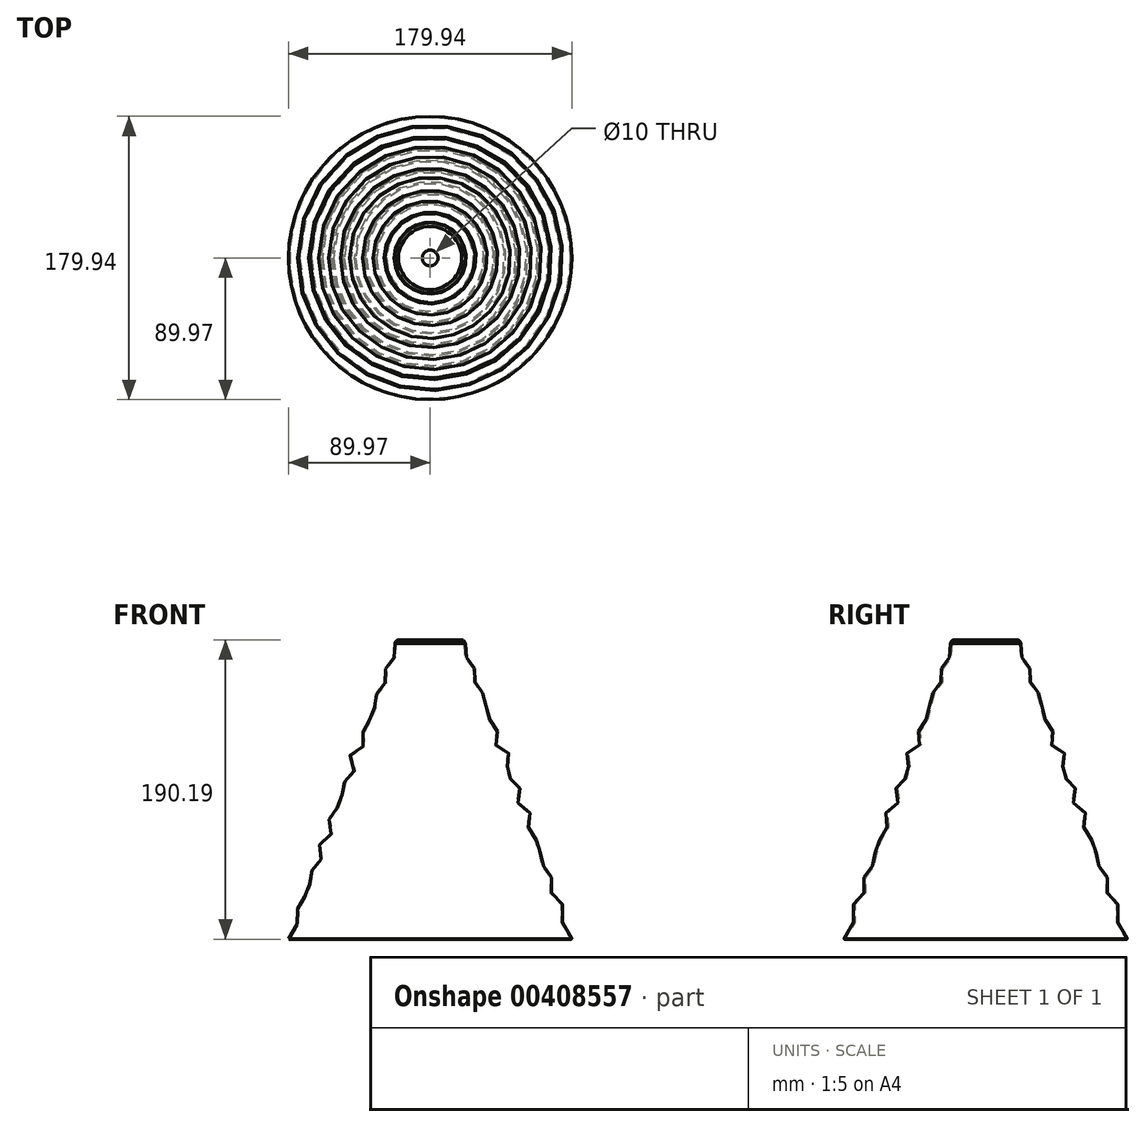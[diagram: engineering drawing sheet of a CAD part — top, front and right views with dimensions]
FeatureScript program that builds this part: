
annotation { "Feature Type Name" : "Feature", "Feature Type Description" : "" }
export const myFeature = defineFeature(function(context is Context, id is Id, definition is map)
    precondition{}
    {
        {
            var Q0;
            Q0=qCreatedBy(makeId("Front.planeOp"),FACE);
            var sketch = newSketch(context, id + "F0", { "sketchPlane" : qUnion([Q0])});
            skLineSegment(sketch, "E0", {"start": v(0, 0) * mm, "end": v(180, 0) * mm, "construction": true});
            skLineSegment(sketch, "E1", {"start": v(180, 0) * mm, "end": v(90, 0) * mm, "construction": true});
            skLineSegment(sketch, "E2", {"start": v(90, 0) * mm, "end": v(90, 190) * mm, "construction": true});
            skLineSegment(sketch, "E3", {"start": v(90, 190) * mm, "end": v(110, 190) * mm, "construction": true});
            skLineSegment(sketch, "E4", {"start": v(90, 190) * mm, "end": v(70, 190) * mm, "construction": true});
            skLineSegment(sketch, "E5", {"start": v(70, 190) * mm, "end": v(85, 190) * mm, "construction": true});
            skLineSegment(sketch, "E6", {"start": v(85, 190) * mm, "end": v(95, 190) * mm, "construction": true});
            skLineSegment(sketch, "E7", {"start": v(70, 190) * mm, "end": v(0, 0) * mm, "construction": true});
            skLineSegment(sketch, "E8", {"start": v(70, 190) * mm, "end": v(90, 244.29) * mm, "construction": true});
            skLineSegment(sketch, "E9", {"start": v(90, 244.29) * mm, "end": v(90, 190) * mm, "construction": true});
            skLineSegment(sketch, "E10", {"start": v(0, 0) * mm, "end": v(0, 244.29) * mm, "construction": true});
            skPoint(sketch, "E11.23.internal.snap0", {"position": v(90, 217.14) * mm});
            skFitSpline(sketch, "E11", {"points": [v(0, 0) * mm, v(6.23, 12.04) * mm, v(6.44, 22.84) * mm, v(13.36, 30.4) * mm, v(13.14, 41.2) * mm, v(20.48, 49.2) * mm, v(19.4, 59.13) * mm, v(27.61, 67.77) * mm, v(25.67, 78.36) * mm, v(34.3, 86.78) * mm, v(33.23, 97.15) * mm, v(41.65, 104.71) * mm, v(39.06, 116.38) * mm, v(48.35, 123.72) * mm, v(47.27, 134.52) * mm, v(54.83, 142.3) * mm, v(53.97, 152.88) * mm, v(61.1, 160.44) * mm, v(61.07, 170.16) * mm, v(66.82, 178.07) * mm, v(67.56, 187.44) * mm, v(73.32, 195.75) * mm, v(73.6, 204.48) * mm, v(82.35, 217.14) * mm, v(81.92, 228.43) * mm, v(87, 236.15) * mm], "startDerivative": vector(195.65, 261.42) * mm, "endDerivative": vector(192.2, 191.7) * mm});
            skLineSegment(sketch, "E12", {"start": v(85, 190) * mm, "end": v(85, 242.54) * mm, "construction": true});
            skFitSpline(sketch, "E13", {"points": [v(67.56, 187.44) * mm, v(68.56, 189.3) * mm, v(70, 190) * mm], "startDerivative": vector(1.51, 4.04) * mm, "endDerivative": vector(3.4, 1) * mm});
            skLineSegment(sketch, "E14", {"start": v(90, 190) * mm, "end": v(90, 170) * mm, "construction": true});
            skLineSegment(sketch, "E15", {"start": v(90, 170) * mm, "end": v(70, 170) * mm, "construction": true});
            skLineSegment(sketch, "E16", {"start": v(70, 170) * mm, "end": v(90, 190) * mm, "construction": true});
            skFitSpline(sketch, "E17", {"points": [v(0.92, 0.04) * mm, v(7.15, 12.08) * mm, v(7.37, 22.88) * mm, v(14.28, 30.45) * mm, v(14.06, 41.25) * mm, v(21.4, 49.24) * mm, v(20.33, 59.18) * mm, v(28.54, 67.82) * mm, v(26.6, 78.4) * mm, v(35.23, 86.83) * mm, v(34.15, 97.2) * mm, v(42.58, 104.75) * mm, v(39.99, 116.42) * mm, v(49.27, 123.76) * mm, v(48.2, 134.57) * mm, v(55.75, 142.34) * mm, v(54.9, 152.93) * mm, v(62.02, 160.49) * mm, v(61.99, 170.2) * mm, v(67.75, 178.1) * mm, v(68.49, 187.49) * mm, v(74.24, 195.79) * mm, v(74.52, 204.52) * mm, v(83.27, 217.19) * mm, v(82.85, 228.48) * mm, v(87.93, 236.2) * mm], "startDerivative": vector(195.65, 261.42) * mm, "endDerivative": vector(192.2, 191.7) * mm});
            skFitSpline(sketch, "E18", {"points": [v(68.49, 187.49) * mm, v(69.48, 189.35) * mm, v(70.92, 190.04) * mm], "startDerivative": vector(1.51, 4.04) * mm, "endDerivative": vector(3.4, 1) * mm});
            skLineSegment(sketch, "E19", {"start": v(69.87, 189.64) * mm, "end": v(85, 189.64) * mm});
            skLineSegment(sketch, "E20", {"start": v(85, 189.64) * mm, "end": v(85, 190) * mm});
            skLineSegment(sketch, "E21", {"start": v(70, 190) * mm, "end": v(85, 190) * mm});
            skFitSpline(sketch, "E22", {"points": [v(0.03, 0.04) * mm, v(0.53, -0.2) * mm, v(0.92, 0.04) * mm], "startDerivative": vector(0.99, -0.7) * mm, "endDerivative": vector(0.8, 0.72) * mm});
            skSolve(sketch);
        }
        {
            var Q0;
            Q0 = qSketchRegion(id + "F0", true);
            var Q1;
            Q1=sQuery(id+"F0.wireOp",EDGE,"E2");
            revolve(context, id + "F1", {"entities" : qUnion([Q0]), "axis" : qUnion([Q1]), "revolveType" : RevolveType.FULL});
        }
    });
